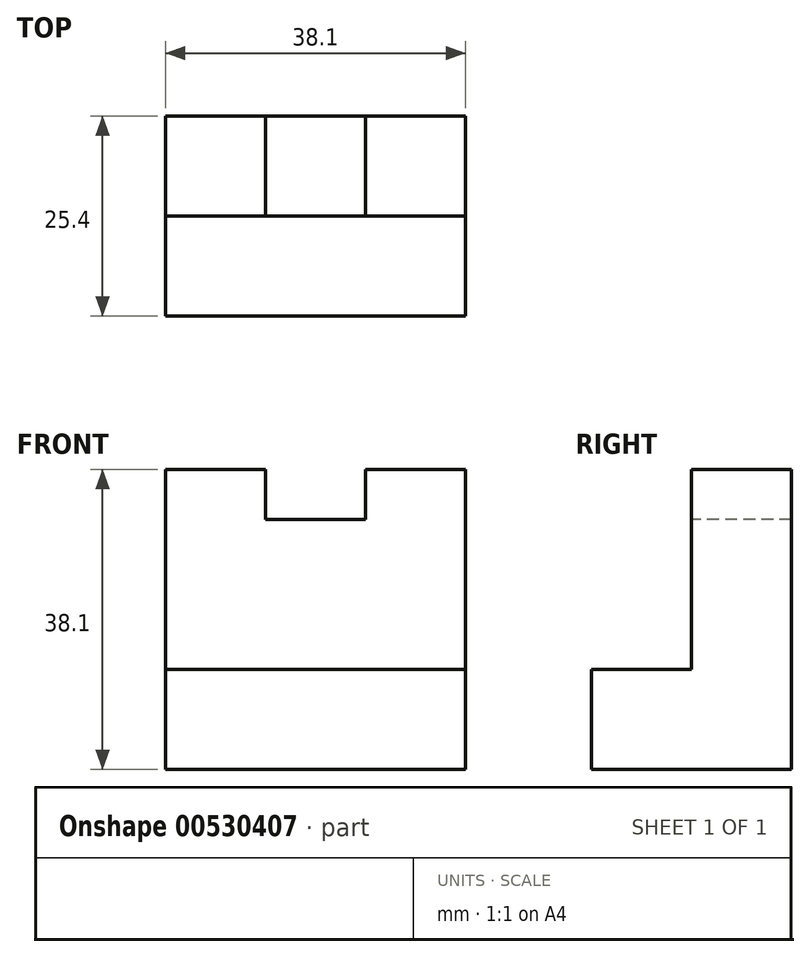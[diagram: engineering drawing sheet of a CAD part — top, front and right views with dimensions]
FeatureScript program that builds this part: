
annotation { "Feature Type Name" : "Feature", "Feature Type Description" : "" }
export const myFeature = defineFeature(function(context is Context, id is Id, definition is map)
    precondition{}
    {
        {
            var Q0;
            Q0=qCreatedBy(makeId("Right.planeOp"),FACE);
            var sketch = newSketch(context, id + "F0", { "sketchPlane" : qUnion([Q0])});
            skLineSegment(sketch, "E0", {"start": v(38.1, 38.1) * mm, "end": v(38.1, 0) * mm});
            skLineSegment(sketch, "E1", {"start": v(12.7, 0) * mm, "end": v(38.1, 0) * mm});
            skLineSegment(sketch, "E2", {"start": v(12.7, 0) * mm, "end": v(12.7, 12.7) * mm});
            skLineSegment(sketch, "E3", {"start": v(12.7, 12.7) * mm, "end": v(25.4, 12.7) * mm});
            skLineSegment(sketch, "E4", {"start": v(25.4, 12.7) * mm, "end": v(25.4, 38.1) * mm});
            skLineSegment(sketch, "E5", {"start": v(25.4, 38.1) * mm, "end": v(38.1, 38.1) * mm});
            skSolve(sketch);
        }
        {
            var Q0;
            Q0=makeQuery(id+"F0.imprint","IMPRINT",FACE,{"disambiguationData":[TD([[makeQuery(id+"F0.imprint","IMPRINT",EDGE,{"derivedFrom":sQuery(id+"F0.wireOp",EDGE,"E0")}),-1.0]])]});
            extrude(context, id + "F1", {"entities" : qUnion([Q0]), "depth" : 38.1 * mm, "offsetDistance" : 25.4 * mm});
        }
        {
            var Q0;
            Q0=makeQuery(id+"F1.opExtrude","SWEPT_FACE",FACE,{"disambiguationData":[OSD([sQuery(id+"F0.wireOp",EDGE,"E4")])]});
            var sketch = newSketch(context, id + "F2", { "sketchPlane" : qUnion([Q0])});
            skLineSegment(sketch, "E6", {"start": v(12.7, 38.1) * mm, "end": v(12.7, 31.75) * mm});
            skLineSegment(sketch, "E7", {"start": v(12.7, 31.75) * mm, "end": v(25.4, 31.75) * mm});
            skLineSegment(sketch, "E8", {"start": v(25.4, 31.75) * mm, "end": v(25.4, 38.1) * mm});
            skSolve(sketch);
        }
        {
            var Q0;
            {var subQ0=sQuery(id+"F2.wireOp",EDGE,"E6");Q0=makeQuery(id+"F2.imprint","IMPRINT",FACE,{"disambiguationData":[TD([[makeQuery(id+"F2.imprint","IMPRINT",EDGE,{"derivedFrom":subQ0}),1.0]])]});}
            extrude(context, id + "F3", {"entities" : qUnion([Q0]), "operationType" : NewBodyOperationType.REMOVE, "oppositeDirection" : true, "depth" : 25.4 * mm, "offsetDistance" : 25.4 * mm});
        }
    });
